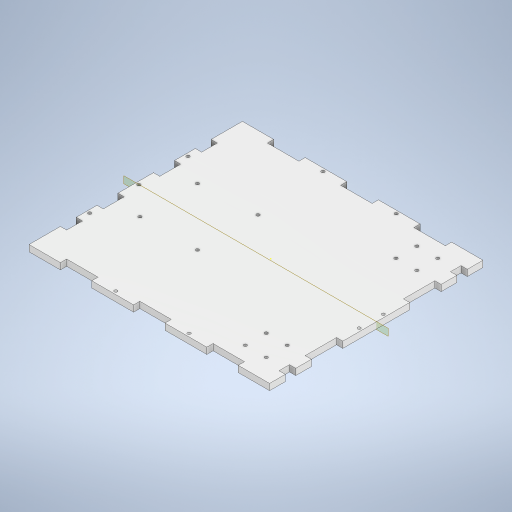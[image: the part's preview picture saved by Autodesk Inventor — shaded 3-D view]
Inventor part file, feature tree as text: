
AUTODESK INVENTOR PART (.ipt)
format: ipt  version: 2024.2 (Build 282272000, 272)  size: 450,048 bytes
history: native  units: mm
features: other x7, sketch x7, extrude x6, reference x6, mirror x1
ambient origin geometry x8: Origin, YZ Plane, XZ Plane, XY Plane, X Axis, Y Axis, Z Axis, Center Point
bodies: Body1 (feature_tree)
feature tree (27):
  other  "Твердое тело1"
  extrude  "Выдавливание1"  Depth=230.0mm
  sketch  "Эскиз2"
  extrude  "Выдавливание3"  Depth=204.0mm
  extrude  "Выдавливание4"  Depth=6.0mm
  other  "РабПлоскость1"
  mirror  "Зеркальное отражение1"
  extrude  "Выдавливание5"  Depth=30.0mm
  extrude  "Выдавливание6"  Depth=30.0mm
  extrude  "Выдавливание7"  Depth=30.0mm
  sketch  "Эскиз1"
  sketch  "Эскиз5"
  sketch  "Эскиз6"
  reference  "Ссылка1"
  reference  "Ссылка2"
  sketch  "Эскиз7"
  reference  "Ссылка3"
  reference  "Ссылка4"
  reference  "Ссылка5"
  reference  "Ссылка6"
  sketch  "Эскиз9"
  sketch  "Эскиз10"
  other  "<userpath>\Documents\Artist-v2\3D\Робот.iam"
  other  "Робот.iam"
  other  "бок:2"
  other  "бок:1"
  other  "перед:1"
